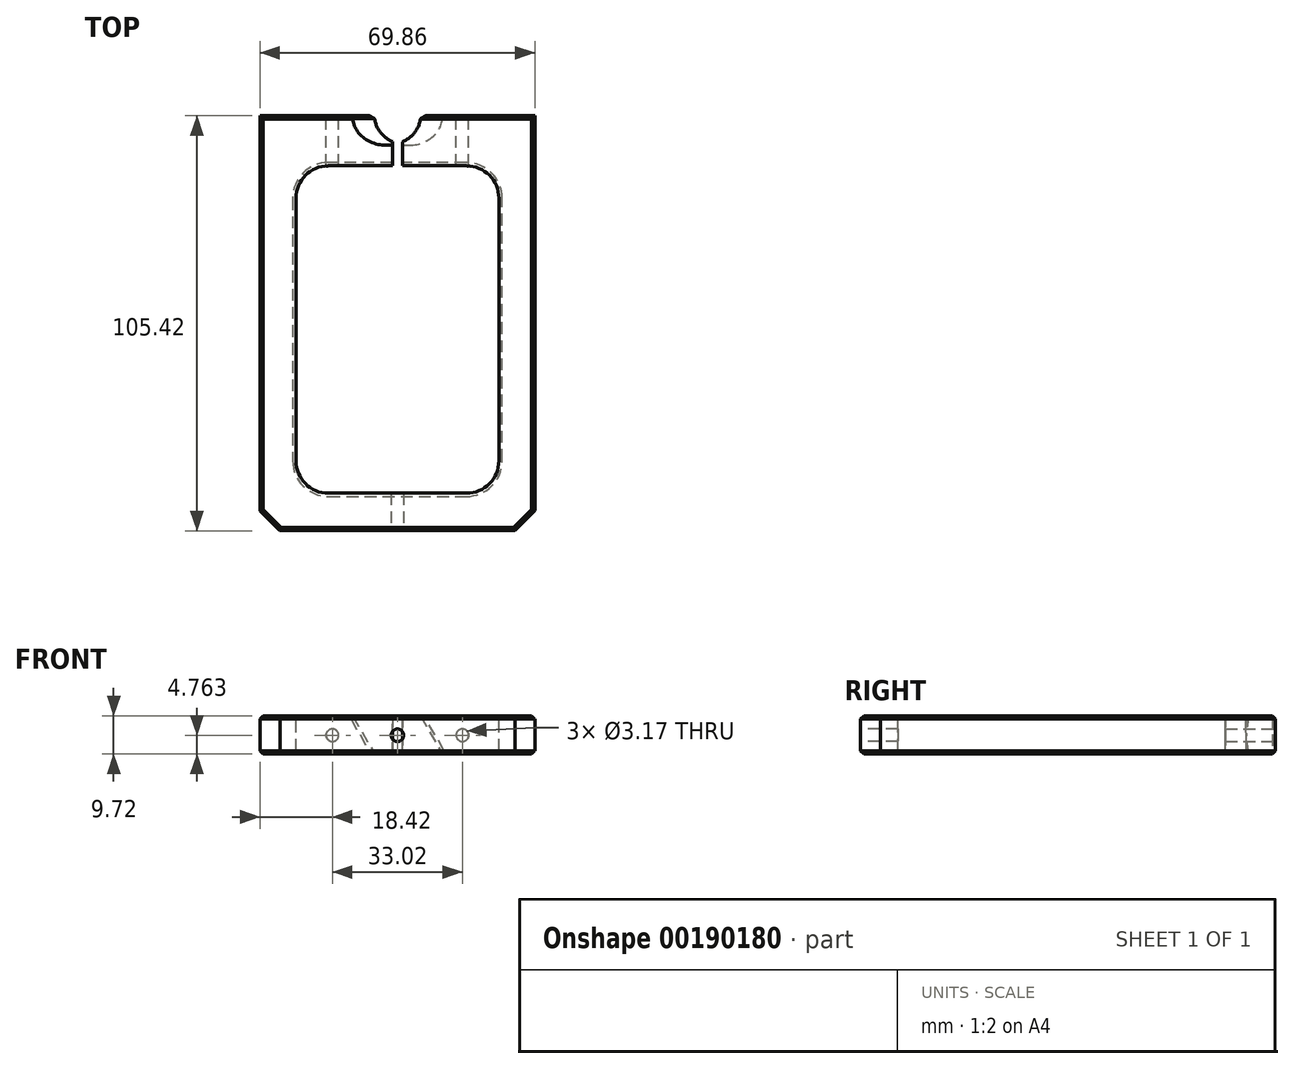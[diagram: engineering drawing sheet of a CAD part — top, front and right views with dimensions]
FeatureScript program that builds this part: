
annotation { "Feature Type Name" : "Feature", "Feature Type Description" : "" }
export const myFeature = defineFeature(function(context is Context, id is Id, definition is map)
    precondition{}
    {
        {
            var Q0;
            Q0=qCreatedBy(makeId("Top.planeOp"),FACE);
            var sketch = newSketch(context, id + "F0", { "sketchPlane" : qUnion([Q0])});
            skLineSegment(sketch, "E0", {"start": v(0, 0) * mm, "end": v(-34.93, 0) * mm});
            skLineSegment(sketch, "E1", {"start": v(-34.93, 0) * mm, "end": v(-34.93, 52.7) * mm});
            skLineSegment(sketch, "E2", {"start": v(-34.93, 52.7) * mm, "end": v(0, 52.7) * mm});
            skLineSegment(sketch, "E3", {"start": v(0, 52.7) * mm, "end": v(0, 0) * mm});
            skLineSegment(sketch, "E4.MirrorCS", {"start": v(-34.93, -52.7) * mm, "end": v(0, -52.7) * mm});
            skLineSegment(sketch, "E5.MirrorCS", {"start": v(-34.93, 0) * mm, "end": v(-34.93, -52.7) * mm});
            skLineSegment(sketch, "E6.MirrorCS", {"start": v(0, -52.7) * mm, "end": v(0, 0) * mm});
            skLineSegment(sketch, "E7.MirrorCS", {"start": v(34.93, 52.7) * mm, "end": v(0, 52.7) * mm});
            skLineSegment(sketch, "E8.MirrorCS", {"start": v(34.93, 0) * mm, "end": v(34.93, 52.7) * mm});
            skLineSegment(sketch, "E9.MirrorCS", {"start": v(34.93, 0) * mm, "end": v(34.93, -52.7) * mm});
            skLineSegment(sketch, "E10.MirrorCS", {"start": v(34.93, -52.7) * mm, "end": v(0, -52.7) * mm});
            skSolve(sketch);
        }
        {
            var Q0;
            Q0=qSketchRegion(id+"F0",true);
            extrude(context, id + "F1", {"entities" : qUnion([Q0]), "depth" : 9.72 * mm});
        }
        {
            var Q0;
            Q0=makeQuery(id+"F1.opExtrude","CAP_FACE",FACE,{"disambiguationData":[OSD([sQuery(id+"F0.wireOp",EDGE,"E1"),sQuery(id+"F0.wireOp",EDGE,"E2"),sQuery(id+"F0.wireOp",EDGE,"E4.MirrorCS"),sQuery(id+"F0.wireOp",EDGE,"E5.MirrorCS"),sQuery(id+"F0.wireOp",EDGE,"E7.MirrorCS"),sQuery(id+"F0.wireOp",EDGE,"E8.MirrorCS"),sQuery(id+"F0.wireOp",EDGE,"E9.MirrorCS"),sQuery(id+"F0.wireOp",EDGE,"E10.MirrorCS")])],"isStart":false});
            var sketch = newSketch(context, id + "F2", { "sketchPlane" : qUnion([Q0])});
            skLineSegment(sketch, "E11", {"start": v(0, 0) * mm, "end": v(-25.78, 0) * mm});
            skLineSegment(sketch, "E12", {"start": v(-25.78, 0) * mm, "end": v(-25.78, 40) * mm});
            skLineSegment(sketch, "E13", {"start": v(-25.78, 40) * mm, "end": v(0, 40) * mm});
            skLineSegment(sketch, "E14", {"start": v(0, 40) * mm, "end": v(0, 0) * mm});
            skLineSegment(sketch, "E15", {"start": v(0, 0) * mm, "end": v(0, -43.18) * mm});
            skLineSegment(sketch, "E16", {"start": v(0, -43.18) * mm, "end": v(-25.78, -43.18) * mm});
            skLineSegment(sketch, "E17", {"start": v(-25.78, -43.18) * mm, "end": v(-25.78, 0) * mm});
            skLineSegment(sketch, "E18.MirrorCS", {"start": v(25.78, 40) * mm, "end": v(0, 40) * mm});
            skLineSegment(sketch, "E19.MirrorCS", {"start": v(25.78, 0) * mm, "end": v(25.78, 40) * mm});
            skLineSegment(sketch, "E20.MirrorCS", {"start": v(25.78, -43.18) * mm, "end": v(25.78, 0) * mm});
            skLineSegment(sketch, "E21.MirrorCS", {"start": v(0, -43.18) * mm, "end": v(25.78, -43.18) * mm});
            skLineSegment(sketch, "E22.MirrorCS", {"start": v(0, 0) * mm, "end": v(25.78, 0) * mm});
            skSolve(sketch);
        }
        {
            var Q0;
            Q0=qSketchRegion(id+"F2",true);
            extrude(context, id + "F3", {"entities" : qUnion([Q0]), "operationType" : NewBodyOperationType.REMOVE, "oppositeDirection" : true, "depth" : 25.4 * mm});
        }
        {
            var Q0;
            Q0=makeQuery(id+"F3.boolean.opBoolean","COPY",EDGE,{"derivedFrom":makeQuery(id+"F3.opExtrude","SWEPT_EDGE",EDGE,{"disambiguationData":[OSD([sQuery(id+"F2.wireOp",EDGE,"E12"),sQuery(id+"F2.wireOp",EDGE,"E13")])]})});
            var Q1;
            Q1=makeQuery(id+"F3.boolean.opBoolean","COPY",EDGE,{"derivedFrom":makeQuery(id+"F3.opExtrude","SWEPT_EDGE",EDGE,{"disambiguationData":[OSD([sQuery(id+"F2.wireOp",EDGE,"E18.MirrorCS"),sQuery(id+"F2.wireOp",EDGE,"E19.MirrorCS")])]})});
            var Q2;
            Q2=makeQuery(id+"F3.boolean.opBoolean","COPY",EDGE,{"derivedFrom":makeQuery(id+"F3.opExtrude","SWEPT_EDGE",EDGE,{"disambiguationData":[OSD([sQuery(id+"F2.wireOp",EDGE,"E16"),sQuery(id+"F2.wireOp",EDGE,"E17")])]})});
            var Q3;
            Q3=makeQuery(id+"F3.boolean.opBoolean","COPY",EDGE,{"derivedFrom":makeQuery(id+"F3.opExtrude","SWEPT_EDGE",EDGE,{"disambiguationData":[OSD([sQuery(id+"F2.wireOp",EDGE,"E20.MirrorCS"),sQuery(id+"F2.wireOp",EDGE,"E21.MirrorCS")])]})});
            fillet(context, id + "F4", {"entities" : qUnion([Q0, Q1, Q2, Q3]), "radius" : 8.25 * mm, "tangentPropagation" : true, "allowEdgeOverflow" : false});
        }
        {
            var Q0;
            Q0=makeQuery(id+"F1.opExtrude","CAP_EDGE",EDGE,{"disambiguationData":[OSD([sQuery(id+"F0.wireOp",EDGE,"E1"),sQuery(id+"F0.wireOp",EDGE,"E5.MirrorCS")])],"isStart":false});
            var Q1;
            Q1=makeQuery(id+"F3.boolean.opBoolean","COPY",EDGE,{"derivedFrom":makeQuery(id+"F3.opExtrude","CAP_EDGE",EDGE,{"disambiguationData":[OSD([sQuery(id+"F2.wireOp",EDGE,"E12"),sQuery(id+"F2.wireOp",EDGE,"E17")])],"isStart":true})});
            var Q2;
            Q2=makeQuery(id+"F1.opExtrude","CAP_EDGE",EDGE,{"disambiguationData":[OSD([sQuery(id+"F0.wireOp",EDGE,"E8.MirrorCS"),sQuery(id+"F0.wireOp",EDGE,"E9.MirrorCS")])],"isStart":false});
            var Q3;
            Q3=makeQuery(id+"F1.opExtrude","CAP_EDGE",EDGE,{"disambiguationData":[OSD([sQuery(id+"F0.wireOp",EDGE,"E4.MirrorCS"),sQuery(id+"F0.wireOp",EDGE,"E10.MirrorCS")])],"isStart":false});
            var Q4;
            {var subQ0=sQuery(id+"F0.wireOp",EDGE,"E7.MirrorCS");var subQ1=sQuery(id+"F0.wireOp",EDGE,"E5.MirrorCS");var subQ2=sQuery(id+"F0.wireOp",EDGE,"E2");var subQ3=sQuery(id+"F0.wireOp",EDGE,"E1");Q4=makeQuery(id+"F3.boolean.opBoolean","SPLIT",EDGE,{"disambiguationData":[TD([makeQuery(id+"F1.opExtrude","SWEPT_FACE",FACE,{"disambiguationData":[OSD([subQ3,subQ1])]})])],"derivedFrom":makeQuery(id+"F1.opExtrude","CAP_EDGE",EDGE,{"disambiguationData":[OSD([subQ2,subQ0])],"isStart":false})});}
            var Q5;
            {var subQ0=sQuery(id+"F0.wireOp",EDGE,"E9.MirrorCS");var subQ1=sQuery(id+"F0.wireOp",EDGE,"E8.MirrorCS");var subQ2=sQuery(id+"F0.wireOp",EDGE,"E7.MirrorCS");var subQ3=sQuery(id+"F0.wireOp",EDGE,"E2");Q5=makeQuery(id+"F3.boolean.opBoolean","SPLIT",EDGE,{"disambiguationData":[TD([makeQuery(id+"F1.opExtrude","SWEPT_FACE",FACE,{"disambiguationData":[OSD([subQ1,subQ0])]})])],"derivedFrom":makeQuery(id+"F1.opExtrude","CAP_EDGE",EDGE,{"disambiguationData":[OSD([subQ3,subQ2])],"isStart":false})});}
            var Q6;
            Q6=makeQuery(id+"F3.boolean.opBoolean","INTERSECT",EDGE,{"disambiguationData":[OD(0.0)],"derivedFrom":[makeQuery(id+"F1.opExtrude","SWEPT_FACE",FACE,{"disambiguationData":[OSD([sQuery(id+"F0.wireOp",EDGE,"E2"),sQuery(id+"F0.wireOp",EDGE,"E7.MirrorCS")])]}),makeQuery(id+"F3.opExtrude","SWEPT_FACE",FACE,{"disambiguationData":[OSD([sQuery(id+"F2.wireOp",EDGE,"xz3gg1sy-TnOw-hOpx-o32f-W6z7Gsooel78")])]})]});
            var Q7;
            Q7=makeQuery(id+"F3.boolean.opBoolean","INTERSECT",EDGE,{"disambiguationData":[OD(1.0)],"derivedFrom":[makeQuery(id+"F1.opExtrude","SWEPT_FACE",FACE,{"disambiguationData":[OSD([sQuery(id+"F0.wireOp",EDGE,"E2"),sQuery(id+"F0.wireOp",EDGE,"E7.MirrorCS")])]}),makeQuery(id+"F3.opExtrude","SWEPT_FACE",FACE,{"disambiguationData":[OSD([sQuery(id+"F2.wireOp",EDGE,"xz3gg1sy-TnOw-hOpx-o32f-W6z7Gsooel78")])]})]});
            var Q8;
            Q8=makeQuery(id+"F1.opExtrude","CAP_EDGE",EDGE,{"disambiguationData":[OSD([sQuery(id+"F0.wireOp",EDGE,"E1"),sQuery(id+"F0.wireOp",EDGE,"E5.MirrorCS")])],"isStart":true});
            var Q9;
            Q9=makeQuery(id+"F1.opExtrude","CAP_EDGE",EDGE,{"disambiguationData":[OSD([sQuery(id+"F0.wireOp",EDGE,"E4.MirrorCS"),sQuery(id+"F0.wireOp",EDGE,"E10.MirrorCS")])],"isStart":true});
            var Q10;
            Q10=makeQuery(id+"F1.opExtrude","CAP_EDGE",EDGE,{"disambiguationData":[OSD([sQuery(id+"F0.wireOp",EDGE,"E8.MirrorCS"),sQuery(id+"F0.wireOp",EDGE,"E9.MirrorCS")])],"isStart":true});
            var Q11;
            Q11=makeQuery(id+"F3.boolean.opBoolean","INTERSECT",EDGE,{"derivedFrom":[makeQuery(id+"F1.opExtrude","CAP_FACE",FACE,{"disambiguationData":[OSD([sQuery(id+"F0.wireOp",EDGE,"E1"),sQuery(id+"F0.wireOp",EDGE,"E2"),sQuery(id+"F0.wireOp",EDGE,"E4.MirrorCS"),sQuery(id+"F0.wireOp",EDGE,"E5.MirrorCS"),sQuery(id+"F0.wireOp",EDGE,"E7.MirrorCS"),sQuery(id+"F0.wireOp",EDGE,"E8.MirrorCS"),sQuery(id+"F0.wireOp",EDGE,"E9.MirrorCS"),sQuery(id+"F0.wireOp",EDGE,"E10.MirrorCS")])],"isStart":true}),makeQuery(id+"F3.opExtrude","SWEPT_FACE",FACE,{"disambiguationData":[OSD([sQuery(id+"F2.wireOp",EDGE,"E19.MirrorCS"),sQuery(id+"F2.wireOp",EDGE,"E20.MirrorCS")])]})]});
            var Q12;
            {var subQ0=sQuery(id+"F0.wireOp",EDGE,"E7.MirrorCS");var subQ1=sQuery(id+"F0.wireOp",EDGE,"E5.MirrorCS");var subQ2=sQuery(id+"F0.wireOp",EDGE,"E2");var subQ3=sQuery(id+"F0.wireOp",EDGE,"E1");Q12=makeQuery(id+"F3.boolean.opBoolean","SPLIT",EDGE,{"disambiguationData":[TD([makeQuery(id+"F1.opExtrude","SWEPT_FACE",FACE,{"disambiguationData":[OSD([subQ3,subQ1])]})])],"derivedFrom":makeQuery(id+"F1.opExtrude","CAP_EDGE",EDGE,{"disambiguationData":[OSD([subQ2,subQ0])],"isStart":true})});}
            var Q13;
            Q13=makeQuery(id+"F3.boolean.opBoolean","INTERSECT",EDGE,{"derivedFrom":[makeQuery(id+"F1.opExtrude","CAP_FACE",FACE,{"disambiguationData":[OSD([sQuery(id+"F0.wireOp",EDGE,"E1"),sQuery(id+"F0.wireOp",EDGE,"E2"),sQuery(id+"F0.wireOp",EDGE,"E4.MirrorCS"),sQuery(id+"F0.wireOp",EDGE,"E5.MirrorCS"),sQuery(id+"F0.wireOp",EDGE,"E7.MirrorCS"),sQuery(id+"F0.wireOp",EDGE,"E8.MirrorCS"),sQuery(id+"F0.wireOp",EDGE,"E9.MirrorCS"),sQuery(id+"F0.wireOp",EDGE,"E10.MirrorCS")])],"isStart":true}),makeQuery(id+"F3.opExtrude","SWEPT_FACE",FACE,{"disambiguationData":[OSD([sQuery(id+"F2.wireOp",EDGE,"xz3gg1sy-TnOw-hOpx-o32f-W6z7Gsooel78")])]})]});
            var Q14;
            {var subQ0=sQuery(id+"F0.wireOp",EDGE,"E9.MirrorCS");var subQ1=sQuery(id+"F0.wireOp",EDGE,"E8.MirrorCS");var subQ2=sQuery(id+"F0.wireOp",EDGE,"E7.MirrorCS");var subQ3=sQuery(id+"F0.wireOp",EDGE,"E2");Q14=makeQuery(id+"F3.boolean.opBoolean","SPLIT",EDGE,{"disambiguationData":[TD([makeQuery(id+"F1.opExtrude","SWEPT_FACE",FACE,{"disambiguationData":[OSD([subQ1,subQ0])]})])],"derivedFrom":makeQuery(id+"F1.opExtrude","CAP_EDGE",EDGE,{"disambiguationData":[OSD([subQ3,subQ2])],"isStart":true})});}
            chamfer(context, id + "F5", {"entities" : qUnion([Q0, Q1, Q2, Q3, Q4, Q5, Q6, Q7, Q8, Q9, Q10, Q11, Q12, Q13, Q14]), "width" : 0.83 * mm, "tangentPropagation" : true});
        }
        {
            var Q0;
            {var subQ1=sQuery(id+"F0.wireOp",EDGE,"E9.MirrorCS");var subQ2=sQuery(id+"F0.wireOp",EDGE,"E8.MirrorCS");var subQ3=sQuery(id+"F0.wireOp",EDGE,"E7.MirrorCS");var subQ6=sQuery(id+"F0.wireOp",EDGE,"E2");Q0=makeQuery(id+"F3.boolean.opBoolean","SPLIT",FACE,{"disambiguationData":[TD([makeQuery(id+"F1.opExtrude","SWEPT_FACE",FACE,{"disambiguationData":[OSD([subQ2,subQ1])]})])],"derivedFrom":makeQuery(id+"F1.opExtrude","SWEPT_FACE",FACE,{"disambiguationData":[OSD([subQ6,subQ3])]})});}
            var sketch = newSketch(context, id + "F6", { "sketchPlane" : qUnion([Q0])});
            skCircle(sketch, "E23", {"center": v(-16.51, 4.76) * mm, "radius": 1.59 * mm});
            skCircle(sketch, "E24.MirrorC", {"center": v(16.51, 4.76) * mm, "radius": 1.59 * mm});
            skSolve(sketch);
        }
        {
            var Q0;
            Q0=qSketchRegion(id+"F6",true);
            extrude(context, id + "F7", {"entities" : qUnion([Q0]), "operationType" : NewBodyOperationType.REMOVE, "oppositeDirection" : true, "depth" : 25.4 * mm});
        }
        {
            var Q0;
            Q0=makeQuery(id+"F1.opExtrude","SWEPT_EDGE",EDGE,{"disambiguationData":[OSD([sQuery(id+"F0.wireOp",EDGE,"E4.MirrorCS"),sQuery(id+"F0.wireOp",EDGE,"E5.MirrorCS")])]});
            var Q1;
            Q1=makeQuery(id+"F1.opExtrude","SWEPT_EDGE",EDGE,{"disambiguationData":[OSD([sQuery(id+"F0.wireOp",EDGE,"E9.MirrorCS"),sQuery(id+"F0.wireOp",EDGE,"E10.MirrorCS")])]});
            chamfer(context, id + "F8", {"entities" : qUnion([Q0, Q1]), "width" : 5.08 * mm, "tangentPropagation" : true});
        }
        {
            var Q0;
            {var subQ0=sQuery(id+"F0.wireOp",EDGE,"E5.MirrorCS");var subQ1=sQuery(id+"F0.wireOp",EDGE,"E4.MirrorCS");Q0=makeQuery(id+"F8.opChamfer","BLEND_EDGE",EDGE,{"blendedFrom":[makeQuery(id+"F1.opExtrude","SWEPT_EDGE",EDGE,{"disambiguationData":[OSD([subQ1,subQ0])]}),makeQuery(id+"F1.opExtrude","CAP_FACE",FACE,{"disambiguationData":[OSD([sQuery(id+"F0.wireOp",EDGE,"E1"),sQuery(id+"F0.wireOp",EDGE,"E2"),subQ1,subQ0,sQuery(id+"F0.wireOp",EDGE,"E7.MirrorCS"),sQuery(id+"F0.wireOp",EDGE,"E8.MirrorCS"),sQuery(id+"F0.wireOp",EDGE,"E9.MirrorCS"),sQuery(id+"F0.wireOp",EDGE,"E10.MirrorCS")])],"isStart":true})],"blendedInto":[makeQuery(id+"F1.opExtrude","CAP_FACE",FACE,{"disambiguationData":[OSD([sQuery(id+"F0.wireOp",EDGE,"E1"),sQuery(id+"F0.wireOp",EDGE,"E2"),subQ1,subQ0,sQuery(id+"F0.wireOp",EDGE,"E7.MirrorCS"),sQuery(id+"F0.wireOp",EDGE,"E8.MirrorCS"),sQuery(id+"F0.wireOp",EDGE,"E9.MirrorCS"),sQuery(id+"F0.wireOp",EDGE,"E10.MirrorCS")])],"isStart":true})]});}
            var Q1;
            {var subQ0=sQuery(id+"F0.wireOp",EDGE,"E10.MirrorCS");var subQ1=sQuery(id+"F0.wireOp",EDGE,"E9.MirrorCS");Q1=makeQuery(id+"F8.opChamfer","BLEND_EDGE",EDGE,{"blendedFrom":[makeQuery(id+"F1.opExtrude","SWEPT_EDGE",EDGE,{"disambiguationData":[OSD([subQ1,subQ0])]}),makeQuery(id+"F1.opExtrude","CAP_FACE",FACE,{"disambiguationData":[OSD([sQuery(id+"F0.wireOp",EDGE,"E1"),sQuery(id+"F0.wireOp",EDGE,"E2"),sQuery(id+"F0.wireOp",EDGE,"E4.MirrorCS"),sQuery(id+"F0.wireOp",EDGE,"E5.MirrorCS"),sQuery(id+"F0.wireOp",EDGE,"E7.MirrorCS"),sQuery(id+"F0.wireOp",EDGE,"E8.MirrorCS"),subQ1,subQ0])],"isStart":true})],"blendedInto":[makeQuery(id+"F1.opExtrude","CAP_FACE",FACE,{"disambiguationData":[OSD([sQuery(id+"F0.wireOp",EDGE,"E1"),sQuery(id+"F0.wireOp",EDGE,"E2"),sQuery(id+"F0.wireOp",EDGE,"E4.MirrorCS"),sQuery(id+"F0.wireOp",EDGE,"E5.MirrorCS"),sQuery(id+"F0.wireOp",EDGE,"E7.MirrorCS"),sQuery(id+"F0.wireOp",EDGE,"E8.MirrorCS"),subQ1,subQ0])],"isStart":true})]});}
            var Q2;
            {var subQ0=sQuery(id+"F0.wireOp",EDGE,"E10.MirrorCS");var subQ1=sQuery(id+"F0.wireOp",EDGE,"E9.MirrorCS");Q2=makeQuery(id+"F8.opChamfer","BLEND_EDGE",EDGE,{"blendedFrom":[makeQuery(id+"F1.opExtrude","SWEPT_EDGE",EDGE,{"disambiguationData":[OSD([subQ1,subQ0])]}),makeQuery(id+"F1.opExtrude","CAP_FACE",FACE,{"disambiguationData":[OSD([sQuery(id+"F0.wireOp",EDGE,"E1"),sQuery(id+"F0.wireOp",EDGE,"E2"),sQuery(id+"F0.wireOp",EDGE,"E4.MirrorCS"),sQuery(id+"F0.wireOp",EDGE,"E5.MirrorCS"),sQuery(id+"F0.wireOp",EDGE,"E7.MirrorCS"),sQuery(id+"F0.wireOp",EDGE,"E8.MirrorCS"),subQ1,subQ0])],"isStart":false})],"blendedInto":[makeQuery(id+"F1.opExtrude","CAP_FACE",FACE,{"disambiguationData":[OSD([sQuery(id+"F0.wireOp",EDGE,"E1"),sQuery(id+"F0.wireOp",EDGE,"E2"),sQuery(id+"F0.wireOp",EDGE,"E4.MirrorCS"),sQuery(id+"F0.wireOp",EDGE,"E5.MirrorCS"),sQuery(id+"F0.wireOp",EDGE,"E7.MirrorCS"),sQuery(id+"F0.wireOp",EDGE,"E8.MirrorCS"),subQ1,subQ0])],"isStart":false})]});}
            var Q3;
            {var subQ0=sQuery(id+"F0.wireOp",EDGE,"E5.MirrorCS");var subQ1=sQuery(id+"F0.wireOp",EDGE,"E4.MirrorCS");Q3=makeQuery(id+"F8.opChamfer","BLEND_EDGE",EDGE,{"blendedFrom":[makeQuery(id+"F1.opExtrude","SWEPT_EDGE",EDGE,{"disambiguationData":[OSD([subQ1,subQ0])]}),makeQuery(id+"F1.opExtrude","CAP_FACE",FACE,{"disambiguationData":[OSD([sQuery(id+"F0.wireOp",EDGE,"E1"),sQuery(id+"F0.wireOp",EDGE,"E2"),subQ1,subQ0,sQuery(id+"F0.wireOp",EDGE,"E7.MirrorCS"),sQuery(id+"F0.wireOp",EDGE,"E8.MirrorCS"),sQuery(id+"F0.wireOp",EDGE,"E9.MirrorCS"),sQuery(id+"F0.wireOp",EDGE,"E10.MirrorCS")])],"isStart":false})],"blendedInto":[makeQuery(id+"F1.opExtrude","CAP_FACE",FACE,{"disambiguationData":[OSD([sQuery(id+"F0.wireOp",EDGE,"E1"),sQuery(id+"F0.wireOp",EDGE,"E2"),subQ1,subQ0,sQuery(id+"F0.wireOp",EDGE,"E7.MirrorCS"),sQuery(id+"F0.wireOp",EDGE,"E8.MirrorCS"),sQuery(id+"F0.wireOp",EDGE,"E9.MirrorCS"),sQuery(id+"F0.wireOp",EDGE,"E10.MirrorCS")])],"isStart":false})]});}
            chamfer(context, id + "F9", {"entities" : qUnion([Q0, Q1, Q2, Q3]), "width" : 0.8 * mm, "tangentPropagation" : true});
        }
        {
            var Q0;
            Q0=makeQuery(id+"F1.opExtrude","SWEPT_FACE",FACE,{"disambiguationData":[OSD([sQuery(id+"F0.wireOp",EDGE,"E4.MirrorCS"),sQuery(id+"F0.wireOp",EDGE,"E10.MirrorCS")])]});
            var sketch = newSketch(context, id + "F10", { "sketchPlane" : qUnion([Q0])});
            skCircle(sketch, "E25", {"center": v(0, 4.76) * mm, "radius": 1.59 * mm});
            skSolve(sketch);
        }
        {
            var Q0;
            Q0=qSketchRegion(id+"F10",true);
            extrude(context, id + "F11", {"entities" : qUnion([Q0]), "operationType" : NewBodyOperationType.REMOVE, "oppositeDirection" : true, "depth" : 25.4 * mm});
        }
        {
            var Q0;
            {var subQ0=sQuery(id+"F0.wireOp",EDGE,"E9.MirrorCS");var subQ1=sQuery(id+"F0.wireOp",EDGE,"E8.MirrorCS");Q0=makeQuery(id+"F5.opChamfer","BLEND_EDGE",EDGE,{"blendedFrom":[makeQuery(id+"F1.opExtrude","CAP_EDGE",EDGE,{"disambiguationData":[OSD([subQ1,subQ0])],"isStart":true}),makeQuery(id+"F1.opExtrude","CAP_FACE",FACE,{"disambiguationData":[OSD([sQuery(id+"F0.wireOp",EDGE,"E1"),sQuery(id+"F0.wireOp",EDGE,"E2"),sQuery(id+"F0.wireOp",EDGE,"E4.MirrorCS"),sQuery(id+"F0.wireOp",EDGE,"E5.MirrorCS"),sQuery(id+"F0.wireOp",EDGE,"E7.MirrorCS"),subQ1,subQ0,sQuery(id+"F0.wireOp",EDGE,"E10.MirrorCS")])],"isStart":true})],"blendedInto":[makeQuery(id+"F1.opExtrude","CAP_FACE",FACE,{"disambiguationData":[OSD([sQuery(id+"F0.wireOp",EDGE,"E1"),sQuery(id+"F0.wireOp",EDGE,"E2"),sQuery(id+"F0.wireOp",EDGE,"E4.MirrorCS"),sQuery(id+"F0.wireOp",EDGE,"E5.MirrorCS"),sQuery(id+"F0.wireOp",EDGE,"E7.MirrorCS"),subQ1,subQ0,sQuery(id+"F0.wireOp",EDGE,"E10.MirrorCS")])],"isStart":true})]});}
            cPlane(context, id + "F12", {"entities" : qUnion([Q0]), "cplaneType" : CPlaneType.LINE_ANGLE, "offset" : 25.4 * mm, "angle" : 30 * degree, "width" : 152.4 * mm, "height" : 152.4 * mm});
        }
        {
            var Q0;
            Q0=qCreatedBy(id+"F12.planeOp",FACE);
            var sketch = newSketch(context, id + "F13", { "sketchPlane" : qUnion([Q0])});
            skCircle(sketch, "E26", {"center": v(2.46, -52.7) * mm, "radius": 7.5 * mm});
            skSolve(sketch);
        }
        {
            var Q0;
            Q0 = qSketchRegion(id + "F13", true);
            var Q1;
            Q1 = qSketchRegion(id + "F2", true);
            extrude(context, id + "F14", {"entities" : qUnion([Q0, Q1]), "operationType" : NewBodyOperationType.REMOVE, "oppositeDirection" : true, "depth" : 50.8 * mm});
        }
        {
            var Q0;
            Q0=makeQuery(id+"F14.boolean.opBoolean","INTERSECT",EDGE,{"disambiguationData":[OD(1.0)],"derivedFrom":[makeQuery(id+"F1.opExtrude","SWEPT_FACE",FACE,{"disambiguationData":[OSD([sQuery(id+"F0.wireOp",EDGE,"E2"),sQuery(id+"F0.wireOp",EDGE,"E7.MirrorCS")])]}),makeQuery(id+"F14.opExtrude","SWEPT_FACE",FACE,{"disambiguationData":[OSD([sQuery(id+"F13.wireOp",EDGE,"E26")])]})]});
            var Q1;
            Q1=makeQuery(id+"F14.boolean.opBoolean","INTERSECT",EDGE,{"disambiguationData":[OD(0.0)],"derivedFrom":[makeQuery(id+"F1.opExtrude","SWEPT_FACE",FACE,{"disambiguationData":[OSD([sQuery(id+"F0.wireOp",EDGE,"E2"),sQuery(id+"F0.wireOp",EDGE,"E7.MirrorCS")])]}),makeQuery(id+"F14.opExtrude","SWEPT_FACE",FACE,{"disambiguationData":[OSD([sQuery(id+"F13.wireOp",EDGE,"E26")])]})]});
            chamfer(context, id + "F15", {"entities" : qUnion([Q0, Q1]), "width" : 0.8 * mm, "tangentPropagation" : true});
        }
        {
            var Q0;
            Q0=makeQuery(id+"F3.boolean.opBoolean","COPY",FACE,{"derivedFrom":makeQuery(id+"F3.opExtrude","SWEPT_FACE",FACE,{"disambiguationData":[OSD([sQuery(id+"F2.wireOp",EDGE,"E13"),sQuery(id+"F2.wireOp",EDGE,"E18.MirrorCS")])]})});
            var sketch = newSketch(context, id + "F16", { "sketchPlane" : qUnion([Q0])});
            skLineSegment(sketch, "E27", {"start": v(-1.27, 12.7) * mm, "end": v(-1.27, -2.54) * mm});
            skLineSegment(sketch, "E28", {"start": v(-1.27, -2.54) * mm, "end": v(1.27, -2.54) * mm});
            skLineSegment(sketch, "E29", {"start": v(1.27, -2.54) * mm, "end": v(1.27, 12.7) * mm});
            skLineSegment(sketch, "E30", {"start": v(1.27, 12.7) * mm, "end": v(-1.27, 12.7) * mm});
            skSolve(sketch);
        }
        {
            var Q0;
            Q0 = qSketchRegion(id + "F16", true);
            extrude(context, id + "F17", {"entities" : qUnion([Q0]), "operationType" : NewBodyOperationType.REMOVE, "oppositeDirection" : true, "depth" : 25.4 * mm});
        }
        {
            var Q0;
            {var subQ0=sQuery(id+"F0.wireOp",EDGE,"E5.MirrorCS");var subQ1=sQuery(id+"F0.wireOp",EDGE,"E1");Q0=makeQuery(id+"F5.opChamfer","BLEND_EDGE",EDGE,{"blendedFrom":[makeQuery(id+"F1.opExtrude","CAP_EDGE",EDGE,{"disambiguationData":[OSD([subQ1,subQ0])],"isStart":true}),makeQuery(id+"F1.opExtrude","CAP_FACE",FACE,{"disambiguationData":[OSD([subQ1,sQuery(id+"F0.wireOp",EDGE,"E2"),sQuery(id+"F0.wireOp",EDGE,"E4.MirrorCS"),subQ0,sQuery(id+"F0.wireOp",EDGE,"E7.MirrorCS"),sQuery(id+"F0.wireOp",EDGE,"E8.MirrorCS"),sQuery(id+"F0.wireOp",EDGE,"E9.MirrorCS"),sQuery(id+"F0.wireOp",EDGE,"E10.MirrorCS")])],"isStart":true})],"blendedInto":[makeQuery(id+"F1.opExtrude","CAP_FACE",FACE,{"disambiguationData":[OSD([subQ1,sQuery(id+"F0.wireOp",EDGE,"E2"),sQuery(id+"F0.wireOp",EDGE,"E4.MirrorCS"),subQ0,sQuery(id+"F0.wireOp",EDGE,"E7.MirrorCS"),sQuery(id+"F0.wireOp",EDGE,"E8.MirrorCS"),sQuery(id+"F0.wireOp",EDGE,"E9.MirrorCS"),sQuery(id+"F0.wireOp",EDGE,"E10.MirrorCS")])],"isStart":true})]});}
            cPlane(context, id + "F18", {"entities" : qUnion([Q0]), "cplaneType" : CPlaneType.LINE_ANGLE, "offset" : 25.4 * mm, "angle" : 30 * degree, "width" : 152.4 * mm, "height" : 152.4 * mm});
        }
    });
